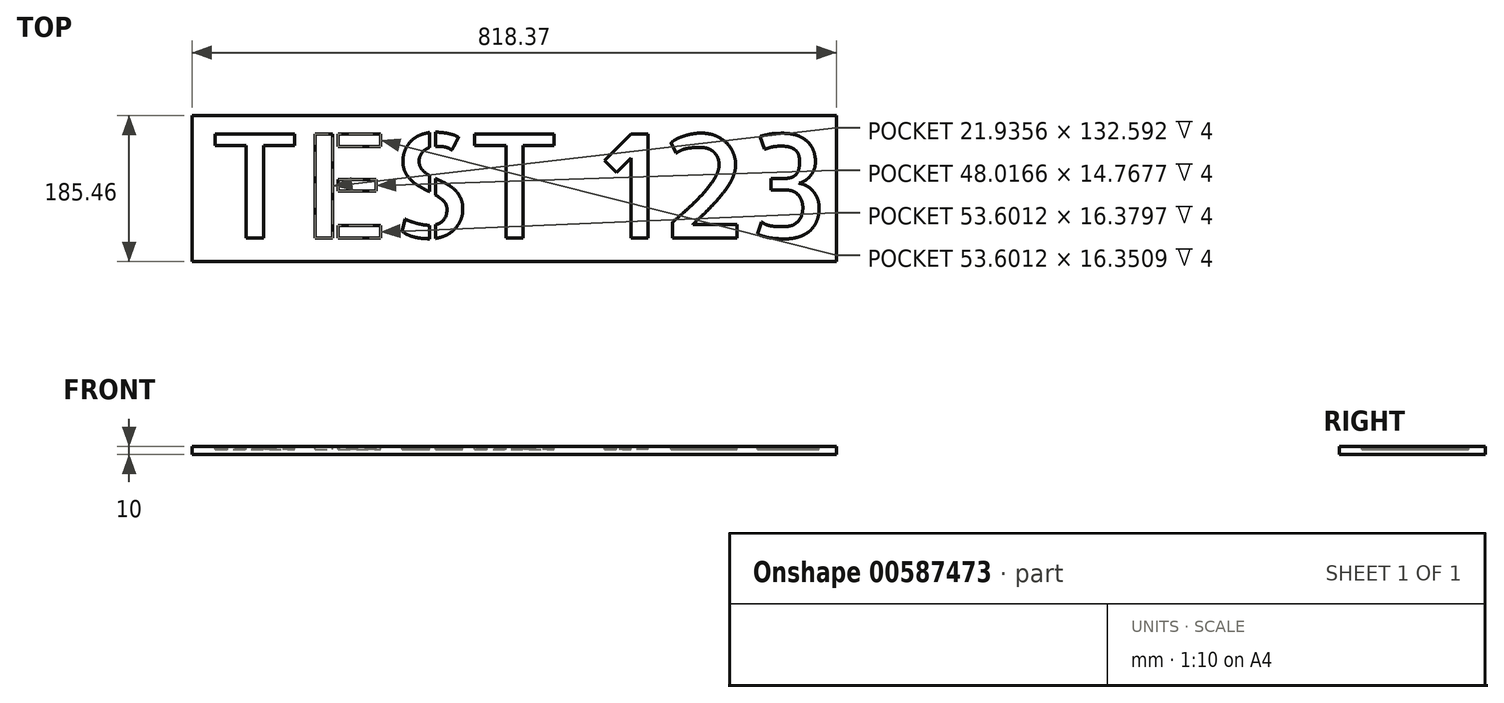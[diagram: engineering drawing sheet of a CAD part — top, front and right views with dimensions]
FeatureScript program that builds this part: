
annotation { "Feature Type Name" : "Feature", "Feature Type Description" : "" }
export const myFeature = defineFeature(function(context is Context, id is Id, definition is map)
    precondition{}
    {
        {
            var Q0;
            Q0=qCreatedBy(makeId("Top.planeOp"),FACE);
            var sketch = newSketch(context, id + "F0", { "sketchPlane" : qUnion([Q0])});
            skLineSegment(sketch, "E0.bottom", {"start": v(-123.66, -69.47) * mm, "end": v(694.71, -69.47) * mm});
            skLineSegment(sketch, "E0.top", {"start": v(-123.66, 115.99) * mm, "end": v(694.71, 115.99) * mm});
            skLineSegment(sketch, "E0.left", {"start": v(-123.66, -69.47) * mm, "end": v(-123.66, 115.99) * mm});
            skLineSegment(sketch, "E0.right", {"start": v(694.71, -69.47) * mm, "end": v(694.71, 115.99) * mm});
            skSolve(sketch);
        }
        {
            var Q0;
            Q0=makeQuery(id+"F0.imprint","IMPRINT",FACE,{"disambiguationData":[TD([[makeQuery(id+"F0.imprint","IMPRINT",EDGE,{"derivedFrom":sQuery(id+"F0.wireOp",EDGE,"E0.bottom")}),1.0]])]});
            extrude(context, id + "F1", {"entities" : qUnion([Q0]), "depth" : 10 * mm, "offsetDistance" : 25 * mm});
        }
        {
            var Q0;
            Q0=makeQuery(id+"F1.opExtrude","CAP_FACE",FACE,{"disambiguationData":[OSD([sQuery(id+"F0.wireOp",EDGE,"E0.bottom"),sQuery(id+"F0.wireOp",EDGE,"E0.top"),sQuery(id+"F0.wireOp",EDGE,"E0.left"),sQuery(id+"F0.wireOp",EDGE,"E0.right")])],"isStart":false});
            var sketch = newSketch(context, id + "F2", { "sketchPlane" : qUnion([Q0])});
            skText(sketch, "E1", { "text": "TEST 123", "fontName": "AllertaStencil-Regular.ttf"});
            const initialGuessF2  = {"E1": [-0.1035, -0.03986, 1, 0, 0.13265]};
            skSetInitialGuess(sketch, initialGuessF2);
            skSolve(sketch);
        }
        {
            var Q0;
            Q0 = qSketchRegion(id + "F2", true);
            extrude(context, id + "F3", {"entities" : qUnion([Q0]), "operationType" : NewBodyOperationType.REMOVE, "oppositeDirection" : true, "depth" : 4 * mm, "offsetDistance" : 25 * mm});
        }
    });
